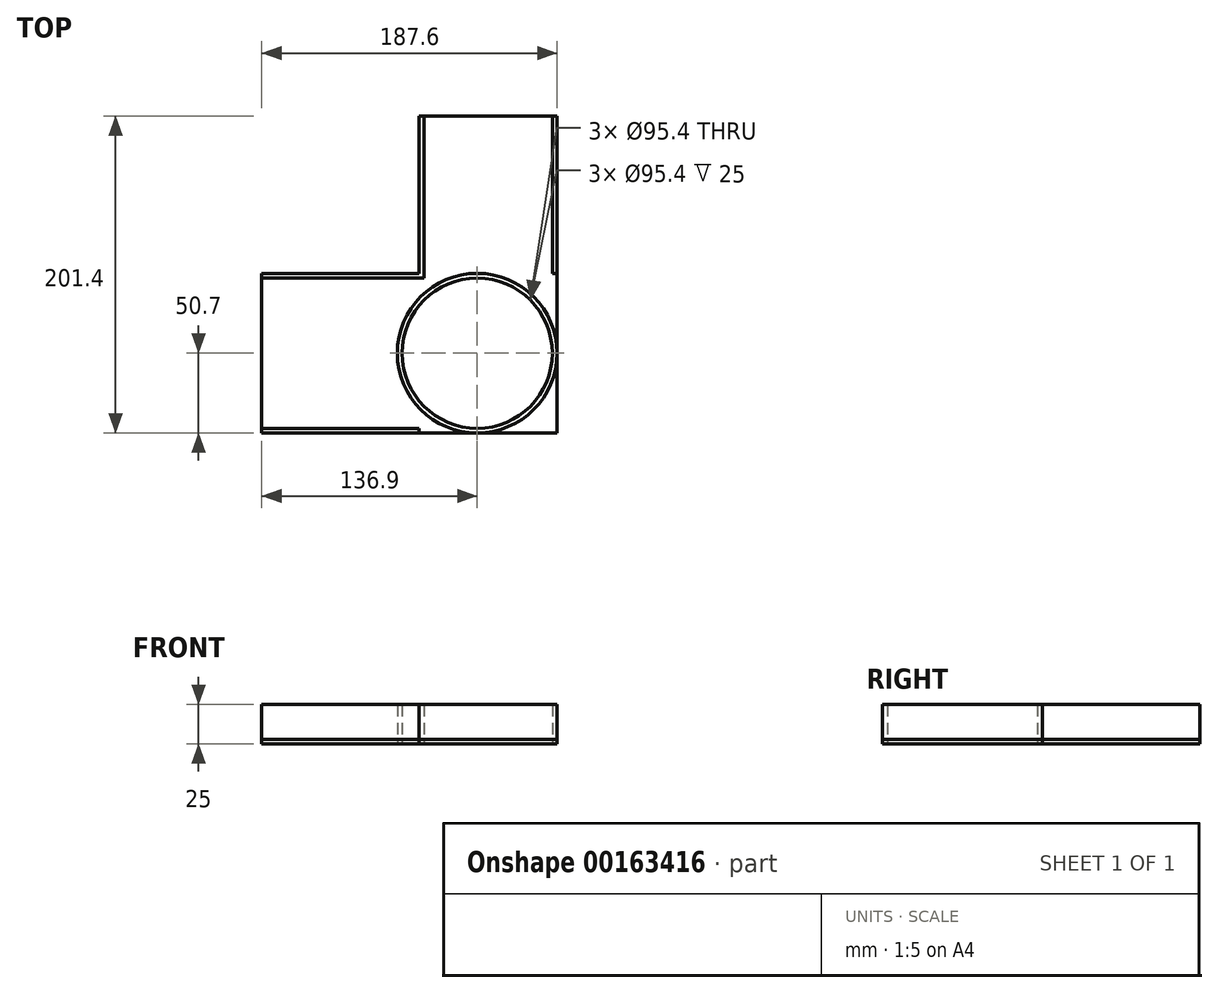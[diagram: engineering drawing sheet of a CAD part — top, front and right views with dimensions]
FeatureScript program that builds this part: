
annotation { "Feature Type Name" : "Feature", "Feature Type Description" : "" }
export const myFeature = defineFeature(function(context is Context, id is Id, definition is map)
    precondition{}
    {
        {
            var Q0;
            Q0=qCreatedBy(makeId("Top.planeOp"),FACE);
            var sketch = newSketch(context, id + "F0", { "sketchPlane" : qUnion([Q0])});
            skCircle(sketch, "E0", {"center": v(0, 0) * mm, "radius": 50.7 * mm});
            skCircle(sketch, "E1", {"center": v(0, 0) * mm, "radius": 47.7 * mm});
            skLineSegment(sketch, "E2", {"start": v(-36.9, -50.7) * mm, "end": v(-136.9, -50.7) * mm});
            skLineSegment(sketch, "E3", {"start": v(-136.9, -50.7) * mm, "end": v(-136.9, -47.7) * mm});
            skLineSegment(sketch, "E4", {"start": v(-136.9, -47.7) * mm, "end": v(-36.9, -47.7) * mm});
            skLineSegment(sketch, "E5", {"start": v(-36.9, -47.7) * mm, "end": v(-36.9, -50.7) * mm});
            skLineSegment(sketch, "E6.MirrorCS", {"start": v(-136.9, 50.7) * mm, "end": v(-136.9, 47.7) * mm});
            skLineSegment(sketch, "E7.MirrorCS", {"start": v(-136.9, 47.7) * mm, "end": v(-36.9, 47.7) * mm});
            skLineSegment(sketch, "E8.MirrorCS", {"start": v(-36.9, 50.7) * mm, "end": v(-136.9, 50.7) * mm});
            skLineSegment(sketch, "E9", {"start": v(-36.9, 50.7) * mm, "end": v(-36.9, 150.7) * mm});
            skLineSegment(sketch, "E10", {"start": v(-36.9, 150.7) * mm, "end": v(-33.9, 150.7) * mm});
            skLineSegment(sketch, "E11", {"start": v(-33.9, 150.7) * mm, "end": v(-33.9, 47.7) * mm});
            skLineSegment(sketch, "E12", {"start": v(-33.9, 47.7) * mm, "end": v(-36.9, 47.7) * mm});
            skLineSegment(sketch, "E13", {"start": v(47.7, 50.7) * mm, "end": v(47.7, 150.7) * mm});
            skLineSegment(sketch, "E14", {"start": v(47.7, 150.7) * mm, "end": v(50.7, 150.7) * mm});
            skLineSegment(sketch, "E15", {"start": v(50.7, 150.7) * mm, "end": v(50.7, 50.7) * mm});
            skLineSegment(sketch, "E16", {"start": v(47.7, 50.7) * mm, "end": v(50.7, 50.7) * mm});
            skLineSegment(sketch, "E17", {"start": v(-136.9, 47.7) * mm, "end": v(-136.9, -47.7) * mm});
            skLineSegment(sketch, "E18", {"start": v(50.7, -50.7) * mm, "end": v(50.7, 50.7) * mm});
            skLineSegment(sketch, "E19", {"start": v(50.7, -50.7) * mm, "end": v(-36.9, -50.7) * mm});
            skLineSegment(sketch, "E20", {"start": v(47.7, 150.7) * mm, "end": v(-33.9, 150.7) * mm});
            skSolve(sketch);
        }
        {
            var Q0;
            Q0=makeQuery(id+"F0.imprint","IMPRINT",FACE,{"disambiguationData":[TD([[makeQuery(id+"F0.imprint","IMPRINT",EDGE,{"derivedFrom":sQuery(id+"F0.wireOp",EDGE,"E0")}),1.0]])]});
            var Q1;
            Q1=makeQuery(id+"F0.imprint","IMPRINT",FACE,{"disambiguationData":[TD([[makeQuery(id+"F0.imprint","IMPRINT",EDGE,{"derivedFrom":sQuery(id+"F0.wireOp",EDGE,"E7.MirrorCS")}),1.0]])]});
            var Q2;
            Q2=makeQuery(id+"F0.imprint","IMPRINT",FACE,{"disambiguationData":[TD([[makeQuery(id+"F0.imprint","IMPRINT",EDGE,{"derivedFrom":sQuery(id+"F0.wireOp",EDGE,"E13")}),-1.0]])]});
            var Q3;
            Q3=makeQuery(id+"F0.imprint","IMPRINT",FACE,{"disambiguationData":[TD([[makeQuery(id+"F0.imprint","IMPRINT",EDGE,{"derivedFrom":sQuery(id+"F0.wireOp",EDGE,"E2")}),-1.0]])]});
            extrude(context, id + "F1", {"entities" : qUnion([Q0, Q1, Q2, Q3]), "depth" : 25 * mm});
        }
        {
            var Q0;
            Q0 = qSketchRegion(id + "F0", true);
            extrude(context, id + "F2", {"entities" : qUnion([Q0]), "depth" : 3 * mm});
        }
    });
